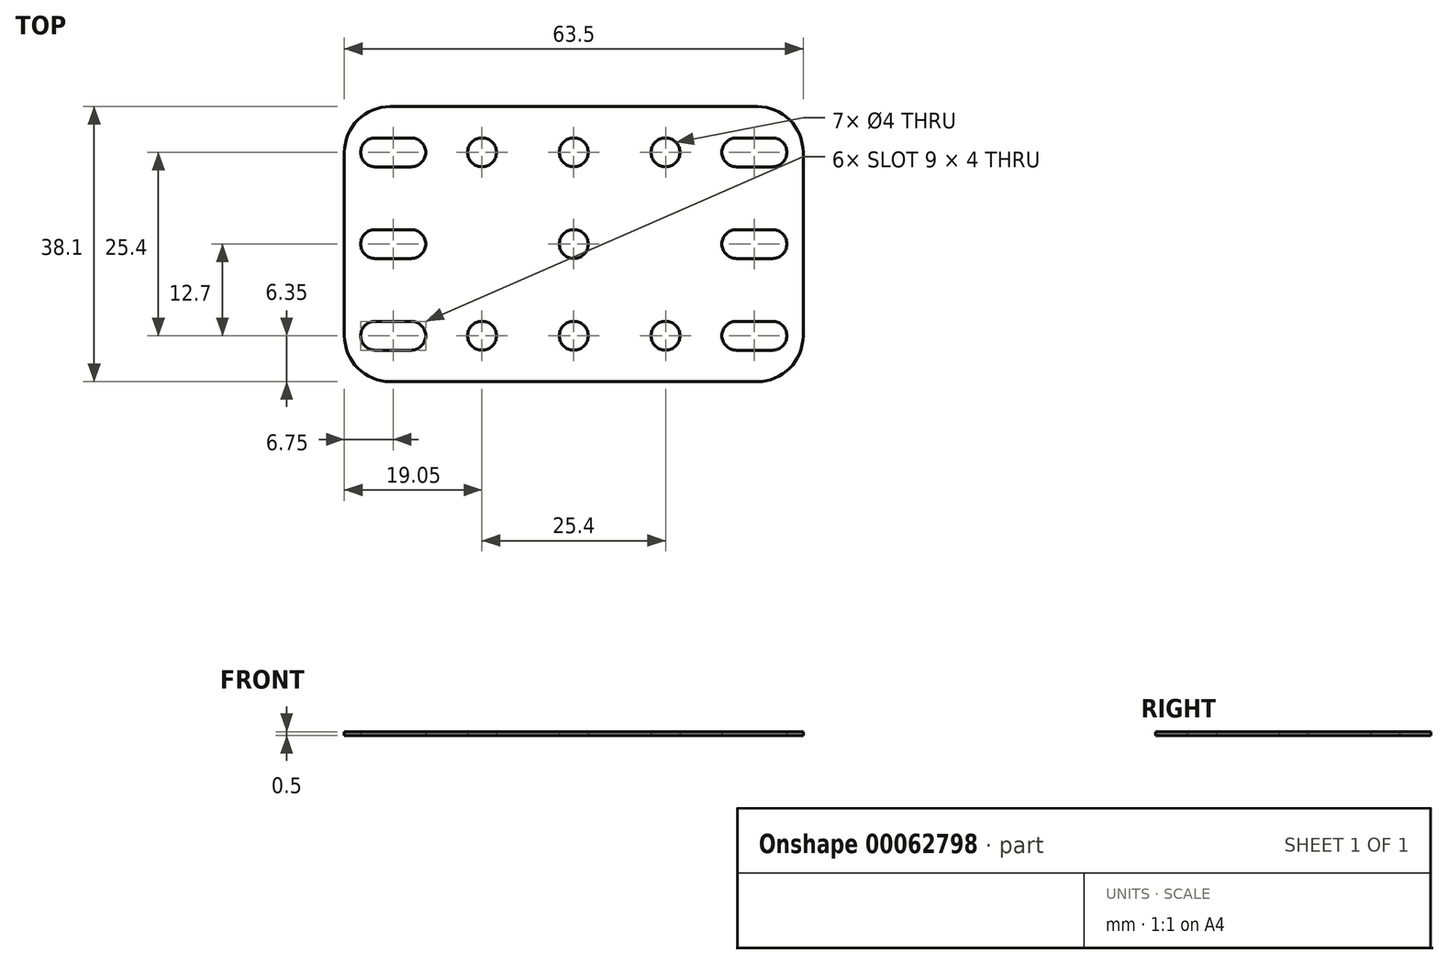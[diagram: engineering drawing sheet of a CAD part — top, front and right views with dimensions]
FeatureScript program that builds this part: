
annotation { "Feature Type Name" : "Feature", "Feature Type Description" : "" }
export const myFeature = defineFeature(function(context is Context, id is Id, definition is map)
    precondition{}
    {
        {
            var Q0;
            Q0=qCreatedBy(makeId("Top.planeOp"),FACE);
            var sketch = newSketch(context, id + "F0", { "sketchPlane" : qUnion([Q0])});
            skLineSegment(sketch, "E0.rect.bottom", {"start": v(25.4, 19.05) * mm, "end": v(-25.4, 19.05) * mm});
            skLineSegment(sketch, "E0.rect.top", {"start": v(25.4, -19.05) * mm, "end": v(-25.4, -19.05) * mm});
            skLineSegment(sketch, "E0.rect.left", {"start": v(31.75, 12.7) * mm, "end": v(31.75, -12.7) * mm});
            skLineSegment(sketch, "E0.rect.right", {"start": v(-31.75, 12.7) * mm, "end": v(-31.75, -12.7) * mm});
            skPoint(sketch, "E0.rect.middle", {"position": v(0, 0) * mm});
            skPoint(sketch, "E1.visualSharp", {"position": v(-31.75, 19.05) * mm});
            skArc(sketch, "E1.filletArc", {"start": v(-25.4, 19.05) * mm, "mid": v(-29.9, 17.2) * mm, "end": v(-31.75, 12.7) * mm});
            skPoint(sketch, "E2.visualSharp", {"position": v(31.75, 19.05) * mm});
            skArc(sketch, "E2.filletArc", {"start": v(31.75, 12.7) * mm, "mid": v(29.9, 17.2) * mm, "end": v(25.4, 19.05) * mm});
            skPoint(sketch, "E3.visualSharp", {"position": v(31.75, -19.05) * mm});
            skArc(sketch, "E3.filletArc", {"start": v(25.4, -19.05) * mm, "mid": v(29.9, -17.2) * mm, "end": v(31.75, -12.7) * mm});
            skPoint(sketch, "E4.visualSharp", {"position": v(-31.75, -19.05) * mm});
            skArc(sketch, "E4.filletArc", {"start": v(-31.75, -12.7) * mm, "mid": v(-29.9, -17.2) * mm, "end": v(-25.4, -19.05) * mm});
            skCircle(sketch, "E5", {"center": v(0, 0) * mm, "radius": 2 * mm});
            skCircle(sketch, "E6.0.1.0", {"center": v(0, 12.7) * mm, "radius": 2 * mm});
            skLineSegment(sketch, "E6.direction1", {"start": v(0, 0) * mm, "end": v(25, 0) * mm, "construction": true});
            skLineSegment(sketch, "E6.direction2", {"start": v(0, 0) * mm, "end": v(0, 12.7) * mm, "construction": true});
            skCircle(sketch, "E7.1.0.0", {"center": v(12.7, 12.7) * mm, "radius": 2 * mm});
            skLineSegment(sketch, "E7.direction1", {"start": v(0, 12.7) * mm, "end": v(12.7, 12.7) * mm, "construction": true});
            skPoint(sketch, "E8.rect.middle", {"position": v(25, 0) * mm});
            skLineSegment(sketch, "E9.rect.bottom", {"start": v(27.5, -2) * mm, "end": v(22.5, -2) * mm});
            skLineSegment(sketch, "E9.rect.top", {"start": v(27.5, 2) * mm, "end": v(22.5, 2) * mm});
            skLineSegment(sketch, "E9.rect.left", {"start": v(29.5, 0) * mm, "end": v(29.5, 0) * mm});
            skLineSegment(sketch, "E9.rect.right", {"start": v(20.5, 0) * mm, "end": v(20.5, 0) * mm});
            skPoint(sketch, "E10.visualSharp", {"position": v(20.5, 2) * mm});
            skArc(sketch, "E10.filletArc", {"start": v(22.5, 2) * mm, "mid": v(21.09, 1.41) * mm, "end": v(20.5, 0) * mm});
            skPoint(sketch, "E11.visualSharp", {"position": v(20.5, -2) * mm});
            skArc(sketch, "E11.filletArc", {"start": v(20.5, 0) * mm, "mid": v(21.09, -1.41) * mm, "end": v(22.5, -2) * mm});
            skPoint(sketch, "E12.visualSharp", {"position": v(29.5, -2) * mm});
            skArc(sketch, "E12.filletArc", {"start": v(27.5, -2) * mm, "mid": v(28.91, -1.41) * mm, "end": v(29.5, 0) * mm});
            skPoint(sketch, "E13.visualSharp", {"position": v(29.5, 2) * mm});
            skArc(sketch, "E13.filletArc", {"start": v(29.5, 0) * mm, "mid": v(28.91, 1.41) * mm, "end": v(27.5, 2) * mm});
            skPoint(sketch, "E14.0.1.0", {"position": v(20.5, 10.7) * mm});
            skPoint(sketch, "E14.0.1.1", {"position": v(25, 12.7) * mm});
            skArc(sketch, "E14.0.1.2", {"start": v(27.5, 10.7) * mm, "mid": v(28.91, 11.29) * mm, "end": v(29.5, 12.7) * mm});
            skPoint(sketch, "E14.0.1.3", {"position": v(29.5, 10.7) * mm});
            skArc(sketch, "E14.0.1.4", {"start": v(20.5, 12.7) * mm, "mid": v(21.09, 11.29) * mm, "end": v(22.5, 10.7) * mm});
            skArc(sketch, "E14.0.1.5", {"start": v(29.5, 12.7) * mm, "mid": v(28.91, 14.11) * mm, "end": v(27.5, 14.7) * mm});
            skPoint(sketch, "E14.0.1.6", {"position": v(29.5, 14.7) * mm});
            skLineSegment(sketch, "E14.0.1.7", {"start": v(27.5, 14.7) * mm, "end": v(22.5, 14.7) * mm});
            skPoint(sketch, "E14.0.1.8", {"position": v(20.5, 14.7) * mm});
            skLineSegment(sketch, "E14.0.1.9", {"start": v(27.5, 10.7) * mm, "end": v(22.5, 10.7) * mm});
            skArc(sketch, "E14.0.1.10", {"start": v(22.5, 14.7) * mm, "mid": v(21.09, 14.11) * mm, "end": v(20.5, 12.7) * mm});
            skPoint(sketch, "E14.0.1.11", {"position": v(25, 12.7) * mm});
            skLineSegment(sketch, "E14.direction1", {"start": v(20.5, -2) * mm, "end": v(45.5, -2) * mm, "construction": true});
            skLineSegment(sketch, "E14.direction2", {"start": v(20.5, -2) * mm, "end": v(20.5, 10.7) * mm, "construction": true});
            skCircle(sketch, "E15.MirrorC", {"center": v(-12.7, 12.7) * mm, "radius": 2 * mm});
            skArc(sketch, "E16.MirrorCS", {"start": v(-29.5, 0) * mm, "mid": v(-28.91, 1.41) * mm, "end": v(-27.5, 2) * mm});
            skLineSegment(sketch, "E17.MirrorCS", {"start": v(-27.5, -2) * mm, "end": v(-22.5, -2) * mm});
            skArc(sketch, "E18.MirrorCS", {"start": v(-20.5, 0) * mm, "mid": v(-21.09, -1.41) * mm, "end": v(-22.5, -2) * mm});
            skArc(sketch, "E19.MirrorCS", {"start": v(-20.5, 12.7) * mm, "mid": v(-21.09, 11.29) * mm, "end": v(-22.5, 10.7) * mm});
            skArc(sketch, "E20.MirrorCS", {"start": v(-22.5, 2) * mm, "mid": v(-21.09, 1.41) * mm, "end": v(-20.5, 0) * mm});
            skArc(sketch, "E21.MirrorCS", {"start": v(-27.5, 10.7) * mm, "mid": v(-28.91, 11.29) * mm, "end": v(-29.5, 12.7) * mm});
            skLineSegment(sketch, "E22.MirrorCS", {"start": v(-27.5, 14.7) * mm, "end": v(-22.5, 14.7) * mm});
            skArc(sketch, "E23.MirrorCS", {"start": v(-22.5, 14.7) * mm, "mid": v(-21.09, 14.11) * mm, "end": v(-20.5, 12.7) * mm});
            skArc(sketch, "E24.MirrorCS", {"start": v(-29.5, 12.7) * mm, "mid": v(-28.91, 14.11) * mm, "end": v(-27.5, 14.7) * mm});
            skArc(sketch, "E25.MirrorCS", {"start": v(-27.5, -2) * mm, "mid": v(-28.91, -1.41) * mm, "end": v(-29.5, 0) * mm});
            skLineSegment(sketch, "E26.MirrorCS", {"start": v(-27.5, 2) * mm, "end": v(-22.5, 2) * mm});
            skPoint(sketch, "E27.MirrorP", {"position": v(-25, 12.7) * mm});
            skPoint(sketch, "E28.MirrorP", {"position": v(-25, 0) * mm});
            skLineSegment(sketch, "E29.MirrorCS", {"start": v(-29.5, 0) * mm, "end": v(-29.5, 0) * mm});
            skPoint(sketch, "E30.MirrorP", {"position": v(-29.5, -2) * mm});
            skLineSegment(sketch, "E31.MirrorCS", {"start": v(-20.5, 0) * mm, "end": v(-20.5, 0) * mm});
            skPoint(sketch, "E32.MirrorP", {"position": v(-20.5, 10.7) * mm});
            skLineSegment(sketch, "E33.MirrorCS", {"start": v(-27.5, 10.7) * mm, "end": v(-22.5, 10.7) * mm});
            skPoint(sketch, "E34.MirrorP", {"position": v(-20.5, 2) * mm});
            skPoint(sketch, "E35.MirrorP", {"position": v(-29.5, 14.7) * mm});
            skPoint(sketch, "E36.MirrorP", {"position": v(-29.5, 10.7) * mm});
            skLineSegment(sketch, "E37.MirrorCS", {"start": v(-20.5, -2) * mm, "end": v(-20.5, 10.7) * mm, "construction": true});
            skPoint(sketch, "E38.MirrorP", {"position": v(-20.5, -2) * mm});
            skPoint(sketch, "E39.MirrorP", {"position": v(-20.5, 14.7) * mm});
            skPoint(sketch, "E40.MirrorP", {"position": v(-29.5, 2) * mm});
            skArc(sketch, "E41.MirrorCS", {"start": v(20.5, -12.7) * mm, "mid": v(21.09, -11.29) * mm, "end": v(22.5, -10.7) * mm});
            skArc(sketch, "E42.MirrorCS", {"start": v(-20.5, -12.7) * mm, "mid": v(-21.09, -11.29) * mm, "end": v(-22.5, -10.7) * mm});
            skArc(sketch, "E43.MirrorCS", {"start": v(-27.5, -10.7) * mm, "mid": v(-28.91, -11.29) * mm, "end": v(-29.5, -12.7) * mm});
            skArc(sketch, "E44.MirrorCS", {"start": v(29.5, -12.7) * mm, "mid": v(28.91, -14.11) * mm, "end": v(27.5, -14.7) * mm});
            skArc(sketch, "E45.MirrorCS", {"start": v(22.5, -14.7) * mm, "mid": v(21.09, -14.11) * mm, "end": v(20.5, -12.7) * mm});
            skArc(sketch, "E46.MirrorCS", {"start": v(-29.5, -12.7) * mm, "mid": v(-28.91, -14.11) * mm, "end": v(-27.5, -14.7) * mm});
            skArc(sketch, "E47.MirrorCS", {"start": v(-22.5, -14.7) * mm, "mid": v(-21.09, -14.11) * mm, "end": v(-20.5, -12.7) * mm});
            skArc(sketch, "E48.MirrorCS", {"start": v(27.5, -10.7) * mm, "mid": v(28.91, -11.29) * mm, "end": v(29.5, -12.7) * mm});
            skPoint(sketch, "E49.MirrorP", {"position": v(25, -12.7) * mm});
            skPoint(sketch, "E50.MirrorP", {"position": v(-25, -12.7) * mm});
            skPoint(sketch, "E51.MirrorP", {"position": v(-20.5, -10.7) * mm});
            skPoint(sketch, "E52.MirrorP", {"position": v(20.5, -14.7) * mm});
            skPoint(sketch, "E53.MirrorP", {"position": v(20.5, -10.7) * mm});
            skPoint(sketch, "E54.MirrorP", {"position": v(-20.5, -14.7) * mm});
            skPoint(sketch, "E55.MirrorP", {"position": v(29.5, -14.7) * mm});
            skPoint(sketch, "E56.MirrorP", {"position": v(-29.5, -14.7) * mm});
            skLineSegment(sketch, "E57.MirrorCS", {"start": v(27.5, -10.7) * mm, "end": v(22.5, -10.7) * mm});
            skLineSegment(sketch, "E58.MirrorCS", {"start": v(-27.5, -10.7) * mm, "end": v(-22.5, -10.7) * mm});
            skCircle(sketch, "E59.MirrorC", {"center": v(-12.7, -12.7) * mm, "radius": 2 * mm});
            skPoint(sketch, "E60.MirrorP", {"position": v(29.5, -10.7) * mm});
            skLineSegment(sketch, "E61.MirrorCS", {"start": v(27.5, -14.7) * mm, "end": v(22.5, -14.7) * mm});
            skLineSegment(sketch, "E62.MirrorCS", {"start": v(-27.5, -14.7) * mm, "end": v(-22.5, -14.7) * mm});
            skLineSegment(sketch, "E63.MirrorCS", {"start": v(0, -12.7) * mm, "end": v(12.7, -12.7) * mm, "construction": true});
            skPoint(sketch, "E64.MirrorP", {"position": v(-29.5, -10.7) * mm});
            skCircle(sketch, "E65.MirrorC", {"center": v(12.7, -12.7) * mm, "radius": 2 * mm});
            skCircle(sketch, "E66.MirrorC", {"center": v(0, -12.7) * mm, "radius": 2 * mm});
            skSolve(sketch);
        }
        {
            var Q0;
            Q0=makeQuery(id+"F0.imprint","IMPRINT",FACE,{"disambiguationData":[TD([[makeQuery(id+"F0.imprint","IMPRINT",EDGE,{"derivedFrom":sQuery(id+"F0.wireOp",EDGE,"E0.rect.bottom")}),1.0]])]});
            extrude(context, id + "F1", {"entities" : qUnion([Q0]), "depth" : 0.5 * mm});
        }
    });
